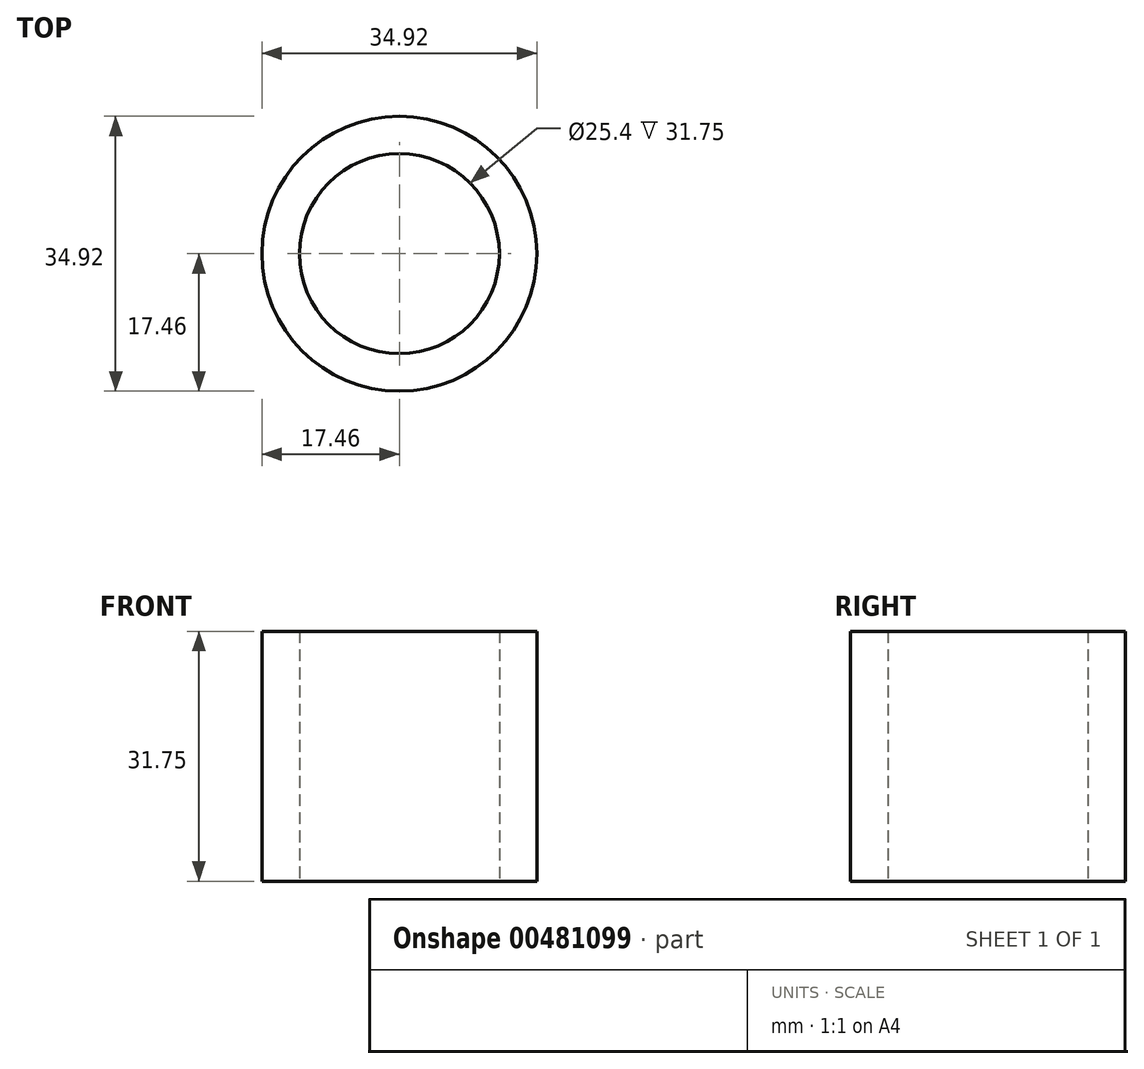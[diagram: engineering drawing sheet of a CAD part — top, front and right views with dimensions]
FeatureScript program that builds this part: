
annotation { "Feature Type Name" : "Feature", "Feature Type Description" : "" }
export const myFeature = defineFeature(function(context is Context, id is Id, definition is map)
    precondition{}
    {
        {
            var Q0;
            Q0=qCreatedBy(makeId("Top.planeOp"),FACE);
            var sketch = newSketch(context, id + "F0", { "sketchPlane" : qUnion([Q0])});
            skCircle(sketch, "E0", {"center": v(0, 0) * mm, "radius": 17.46 * mm});
            skCircle(sketch, "E1", {"center": v(0, 0) * mm, "radius": 12.7 * mm});
            skSolve(sketch);
        }
        {
            var Q0;
            Q0 = qSketchRegion(id + "F0", true);
            extrude(context, id + "F1", {"entities" : qUnion([Q0]), "depth" : 31.75 * mm});
        }
    });
